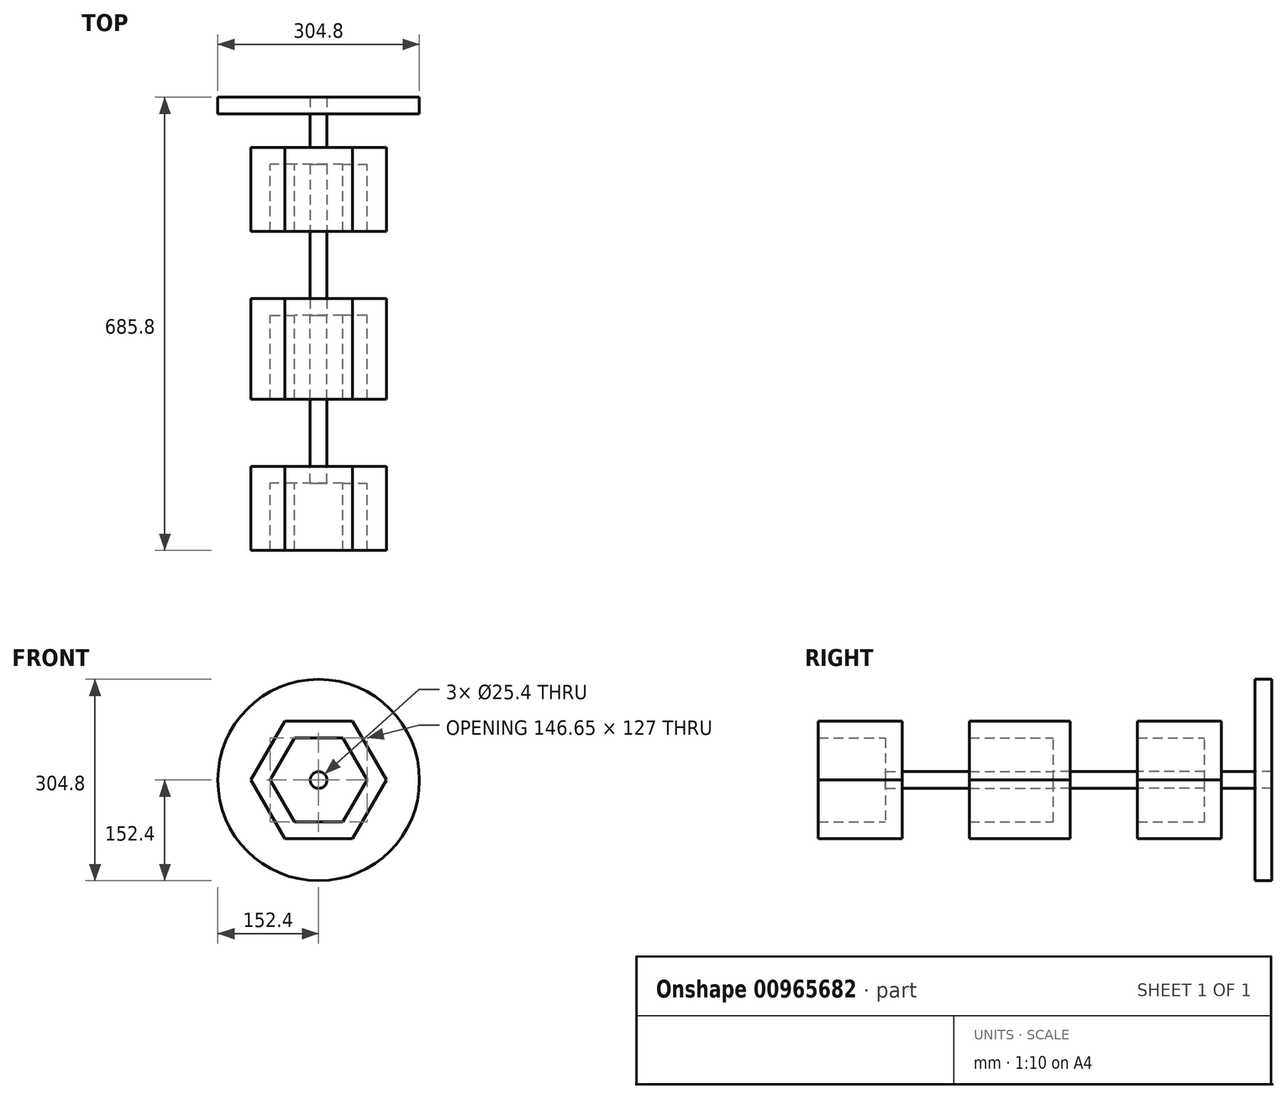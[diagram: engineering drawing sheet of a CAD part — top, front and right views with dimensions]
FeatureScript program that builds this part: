
annotation { "Feature Type Name" : "Feature", "Feature Type Description" : "" }
export const myFeature = defineFeature(function(context is Context, id is Id, definition is map)
    precondition{}
    {
        {
            var Q0;
            Q0=qCreatedBy(makeId("Front.planeOp"),FACE);
            var sketch = newSketch(context, id + "F0", { "sketchPlane" : qUnion([Q0])});
            skCircle(sketch, "E0", {"center": v(0, 0) * mm, "radius": 88.9 * mm});
            skCircle(sketch, "E1.cCircle", {"center": v(0, 0) * mm, "radius": 88.9 * mm, "construction": true});
            skLineSegment(sketch, "E1.0", {"start": v(51.33, -88.9) * mm, "end": v(-51.33, -88.9) * mm});
            skLineSegment(sketch, "E1.1", {"start": v(-51.33, -88.9) * mm, "end": v(-102.65, 0) * mm});
            skLineSegment(sketch, "E1.2", {"start": v(-102.65, 0) * mm, "end": v(-51.33, 88.9) * mm});
            skLineSegment(sketch, "E1.3", {"start": v(-51.33, 88.9) * mm, "end": v(51.33, 88.9) * mm});
            skLineSegment(sketch, "E1.4", {"start": v(51.33, 88.9) * mm, "end": v(102.65, 0) * mm});
            skLineSegment(sketch, "E1.5", {"start": v(102.65, 0) * mm, "end": v(51.33, -88.9) * mm});
            skPoint(sketch, "E1.0.midPoint", {"position": v(0, -88.9) * mm});
            skLineSegment(sketch, "E2.0", {"start": v(-36.66, 63.5) * mm, "end": v(36.66, 63.5) * mm});
            skLineSegment(sketch, "E3.0", {"start": v(36.66, 63.5) * mm, "end": v(73.32, 0) * mm});
            skLineSegment(sketch, "E4.0", {"start": v(73.32, 0) * mm, "end": v(36.66, -63.5) * mm});
            skLineSegment(sketch, "E5.0", {"start": v(36.66, -63.5) * mm, "end": v(-36.66, -63.5) * mm});
            skLineSegment(sketch, "E6.0", {"start": v(-36.66, -63.5) * mm, "end": v(-73.32, 0) * mm});
            skLineSegment(sketch, "E7.0", {"start": v(-73.32, 0) * mm, "end": v(-36.66, 63.5) * mm});
            skCircle(sketch, "E8", {"center": v(0, 0) * mm, "radius": 12.7 * mm});
            skSolve(sketch);
        }
        {
            var Q0;
            Q0 = qSketchRegion(id + "F0", true);
            var Q1;
            Q1=makeQuery(id+"F0.imprint","IMPRINT",FACE,{"disambiguationData":[TD([[makeQuery(id+"F0.imprint","IMPRINT",EDGE,{"derivedFrom":sQuery(id+"F0.wireOp",EDGE,"E2.0")}),-1.0]])]});
            extrude(context, id + "F1", {"entities" : qUnion([Q0, Q1]), "oppositeDirection" : true, "depth" : 25.4 * mm, "offsetDistance" : 25.4 * mm});
        }
        {
            var Q0;
            {var subQ0=sQuery(id+"F0.wireOp",EDGE,"E1.3");var subQ1=sQuery(id+"F0.wireOp",EDGE,"E0");var subQ2=makeQuery(id+"F0.imprint","INTERSECT",VERTEX,{"derivedFrom":[subQ1,subQ0]});Q0=makeQuery(id+"F0.imprint","IMPRINT",FACE,{"disambiguationData":[TD([[makeQuery(id+"F0.imprint","IMPRINT",EDGE,{"disambiguationData":[TD([[subQ2,-1.0]])],"derivedFrom":subQ1}),-1.0]])]});}
            var Q1;
            {var subQ0=sQuery(id+"F0.wireOp",EDGE,"E1.3");var subQ1=sQuery(id+"F0.wireOp",EDGE,"E0");var subQ2=makeQuery(id+"F0.imprint","INTERSECT",VERTEX,{"derivedFrom":[subQ1,subQ0]});Q1=makeQuery(id+"F0.imprint","IMPRINT",FACE,{"disambiguationData":[TD([[makeQuery(id+"F0.imprint","IMPRINT",EDGE,{"disambiguationData":[TD([[subQ2,1.0]])],"derivedFrom":subQ1}),-1.0]])]});}
            var Q2;
            {var subQ0=sQuery(id+"F0.wireOp",EDGE,"E1.4");var subQ1=sQuery(id+"F0.wireOp",EDGE,"E0");var subQ2=makeQuery(id+"F0.imprint","INTERSECT",VERTEX,{"derivedFrom":[subQ1,subQ0]});Q2=makeQuery(id+"F0.imprint","IMPRINT",FACE,{"disambiguationData":[TD([[makeQuery(id+"F0.imprint","IMPRINT",EDGE,{"disambiguationData":[TD([[subQ2,1.0]])],"derivedFrom":subQ1}),-1.0]])]});}
            var Q3;
            {var subQ0=sQuery(id+"F0.wireOp",EDGE,"E1.0");var subQ1=sQuery(id+"F0.wireOp",EDGE,"E0");var subQ2=makeQuery(id+"F0.imprint","INTERSECT",VERTEX,{"derivedFrom":[subQ1,subQ0]});Q3=makeQuery(id+"F0.imprint","IMPRINT",FACE,{"disambiguationData":[TD([[makeQuery(id+"F0.imprint","IMPRINT",EDGE,{"disambiguationData":[TD([[subQ2,-1.0]])],"derivedFrom":subQ1}),-1.0]])]});}
            var Q4;
            {var subQ0=sQuery(id+"F0.wireOp",EDGE,"E1.1");var subQ1=sQuery(id+"F0.wireOp",EDGE,"E0");var subQ2=makeQuery(id+"F0.imprint","INTERSECT",VERTEX,{"derivedFrom":[subQ1,subQ0]});Q4=makeQuery(id+"F0.imprint","IMPRINT",FACE,{"disambiguationData":[TD([[makeQuery(id+"F0.imprint","IMPRINT",EDGE,{"disambiguationData":[TD([[subQ2,-1.0]])],"derivedFrom":subQ1}),-1.0]])]});}
            var Q5;
            {var subQ0=sQuery(id+"F0.wireOp",EDGE,"E1.2");var subQ1=sQuery(id+"F0.wireOp",EDGE,"E0");var subQ2=makeQuery(id+"F0.imprint","INTERSECT",VERTEX,{"derivedFrom":[subQ1,subQ0]});Q5=makeQuery(id+"F0.imprint","IMPRINT",FACE,{"disambiguationData":[TD([[makeQuery(id+"F0.imprint","IMPRINT",EDGE,{"disambiguationData":[TD([[subQ2,-1.0]])],"derivedFrom":subQ1}),-1.0]])]});}
            var Q6;
            Q6=makeQuery(id+"F0.imprint","IMPRINT",FACE,{"disambiguationData":[TD([[makeQuery(id+"F0.imprint","IMPRINT",EDGE,{"derivedFrom":sQuery(id+"F0.wireOp",EDGE,"E2.0")}),1.0]])]});
            extrude(context, id + "F2", {"entities" : qUnion([Q0, Q1, Q2, Q3, Q4, Q5, Q6]), "operationType" : NewBodyOperationType.ADD, "depth" : 127 * mm, "offsetDistance" : 25.4 * mm});
        }
        {
            var Q0;
            Q0=makeQuery(id+"F0.imprint","IMPRINT",FACE,{"disambiguationData":[TD([[makeQuery(id+"F0.imprint","IMPRINT",EDGE,{"derivedFrom":sQuery(id+"F0.wireOp",EDGE,"E8")}),1.0]])]});
            extrude(context, id + "F3", {"entities" : qUnion([Q0]), "depth" : 228.6 * mm, "offsetDistance" : 25.4 * mm});
        }
        {
            var Q0;
            Q0=makeQuery(id+"F3.opExtrude","CAP_FACE",FACE,{"disambiguationData":[OSD([sQuery(id+"F0.wireOp",EDGE,"E8")])],"isStart":false});
            var sketch = newSketch(context, id + "F4", { "sketchPlane" : qUnion([Q0])});
            skCircle(sketch, "E9", {"center": v(0, 0) * mm, "radius": 88.9 * mm});
            skCircle(sketch, "E10.cCircle", {"center": v(0, 0) * mm, "radius": 88.9 * mm, "construction": true});
            skLineSegment(sketch, "E10.0", {"start": v(51.33, -88.9) * mm, "end": v(-51.33, -88.9) * mm});
            skLineSegment(sketch, "E10.1", {"start": v(-51.33, -88.9) * mm, "end": v(-102.65, 0) * mm});
            skLineSegment(sketch, "E10.2", {"start": v(-102.65, 0) * mm, "end": v(-51.33, 88.9) * mm});
            skLineSegment(sketch, "E10.3", {"start": v(-51.33, 88.9) * mm, "end": v(51.33, 88.9) * mm});
            skLineSegment(sketch, "E10.4", {"start": v(51.33, 88.9) * mm, "end": v(102.65, 0) * mm});
            skLineSegment(sketch, "E10.5", {"start": v(102.65, 0) * mm, "end": v(51.33, -88.9) * mm});
            skPoint(sketch, "E10.0.midPoint", {"position": v(0, -88.9) * mm});
            skLineSegment(sketch, "E11.0", {"start": v(-36.66, 63.5) * mm, "end": v(36.66, 63.5) * mm});
            skLineSegment(sketch, "E12.0", {"start": v(36.66, 63.5) * mm, "end": v(73.32, 0) * mm});
            skLineSegment(sketch, "E13.0", {"start": v(73.32, 0) * mm, "end": v(36.66, -63.5) * mm});
            skLineSegment(sketch, "E14.0", {"start": v(36.66, -63.5) * mm, "end": v(-36.66, -63.5) * mm});
            skLineSegment(sketch, "E15.0", {"start": v(-36.66, -63.5) * mm, "end": v(-73.32, 0) * mm});
            skLineSegment(sketch, "E16.0", {"start": v(-73.32, 0) * mm, "end": v(-36.66, 63.5) * mm});
            skSolve(sketch);
        }
        {
            var Q0;
            Q0=makeQuery(id+"F4.imprint","IMPRINT",FACE,{"disambiguationData":[TD([[makeQuery(id+"F4.imprint","IMPRINT",EDGE,{"derivedFrom":sQuery(id+"F4.wireOp",EDGE,"E11.0")}),1.0]])]});
            var Q1;
            Q1=makeQuery(id+"F4.imprint","IMPRINT",FACE,{"disambiguationData":[TD([[makeQuery(id+"F4.imprint","IMPRINT",EDGE,{"derivedFrom":sQuery(id+"F4.wireOp",EDGE,"E11.0")}),-1.0]])]});
            extrude(context, id + "F5", {"entities" : qUnion([Q0, Q1]), "depth" : 25.4 * mm, "offsetDistance" : 25.4 * mm});
        }
        {
            var Q0;
            {var subQ0=sQuery(id+"F4.wireOp",EDGE,"E10.3");var subQ1=sQuery(id+"F4.wireOp",EDGE,"E9");var subQ2=makeQuery(id+"F4.imprint","INTERSECT",VERTEX,{"derivedFrom":[subQ1,subQ0]});Q0=makeQuery(id+"F4.imprint","IMPRINT",FACE,{"disambiguationData":[TD([[makeQuery(id+"F4.imprint","IMPRINT",EDGE,{"disambiguationData":[TD([[subQ2,-1.0]])],"derivedFrom":subQ1}),-1.0]])]});}
            var Q1;
            {var subQ0=sQuery(id+"F4.wireOp",EDGE,"E10.3");var subQ1=sQuery(id+"F4.wireOp",EDGE,"E9");var subQ2=makeQuery(id+"F4.imprint","INTERSECT",VERTEX,{"derivedFrom":[subQ1,subQ0]});Q1=makeQuery(id+"F4.imprint","IMPRINT",FACE,{"disambiguationData":[TD([[makeQuery(id+"F4.imprint","IMPRINT",EDGE,{"disambiguationData":[TD([[subQ2,1.0]])],"derivedFrom":subQ1}),-1.0]])]});}
            var Q2;
            {var subQ0=sQuery(id+"F4.wireOp",EDGE,"E10.4");var subQ1=sQuery(id+"F4.wireOp",EDGE,"E9");var subQ2=makeQuery(id+"F4.imprint","INTERSECT",VERTEX,{"derivedFrom":[subQ1,subQ0]});Q2=makeQuery(id+"F4.imprint","IMPRINT",FACE,{"disambiguationData":[TD([[makeQuery(id+"F4.imprint","IMPRINT",EDGE,{"disambiguationData":[TD([[subQ2,1.0]])],"derivedFrom":subQ1}),-1.0]])]});}
            var Q3;
            {var subQ0=sQuery(id+"F4.wireOp",EDGE,"E10.0");var subQ1=sQuery(id+"F4.wireOp",EDGE,"E9");var subQ2=makeQuery(id+"F4.imprint","INTERSECT",VERTEX,{"derivedFrom":[subQ1,subQ0]});Q3=makeQuery(id+"F4.imprint","IMPRINT",FACE,{"disambiguationData":[TD([[makeQuery(id+"F4.imprint","IMPRINT",EDGE,{"disambiguationData":[TD([[subQ2,-1.0]])],"derivedFrom":subQ1}),-1.0]])]});}
            var Q4;
            {var subQ0=sQuery(id+"F4.wireOp",EDGE,"E10.1");var subQ1=sQuery(id+"F4.wireOp",EDGE,"E9");var subQ2=makeQuery(id+"F4.imprint","INTERSECT",VERTEX,{"derivedFrom":[subQ1,subQ0]});Q4=makeQuery(id+"F4.imprint","IMPRINT",FACE,{"disambiguationData":[TD([[makeQuery(id+"F4.imprint","IMPRINT",EDGE,{"disambiguationData":[TD([[subQ2,-1.0]])],"derivedFrom":subQ1}),-1.0]])]});}
            var Q5;
            {var subQ0=sQuery(id+"F4.wireOp",EDGE,"E10.2");var subQ1=sQuery(id+"F4.wireOp",EDGE,"E9");var subQ2=makeQuery(id+"F4.imprint","INTERSECT",VERTEX,{"derivedFrom":[subQ1,subQ0]});Q5=makeQuery(id+"F4.imprint","IMPRINT",FACE,{"disambiguationData":[TD([[makeQuery(id+"F4.imprint","IMPRINT",EDGE,{"disambiguationData":[TD([[subQ2,-1.0]])],"derivedFrom":subQ1}),-1.0]])]});}
            var Q6;
            Q6=makeQuery(id+"F4.imprint","IMPRINT",FACE,{"disambiguationData":[TD([[makeQuery(id+"F4.imprint","IMPRINT",EDGE,{"derivedFrom":sQuery(id+"F4.wireOp",EDGE,"E11.0")}),1.0]])]});
            extrude(context, id + "F6", {"entities" : qUnion([Q0, Q1, Q2, Q3, Q4, Q5, Q6]), "operationType" : NewBodyOperationType.ADD, "depth" : 127 * mm, "offsetDistance" : 25.4 * mm});
        }
        {
            var Q0;
            Q0=makeQuery(id+"F1.opExtrude","CAP_FACE",FACE,{"disambiguationData":[OSD([sQuery(id+"F0.wireOp",EDGE,"E1.0"),sQuery(id+"F0.wireOp",EDGE,"E1.1"),sQuery(id+"F0.wireOp",EDGE,"E1.2"),sQuery(id+"F0.wireOp",EDGE,"E1.3"),sQuery(id+"F0.wireOp",EDGE,"E1.4"),sQuery(id+"F0.wireOp",EDGE,"E1.5"),sQuery(id+"F0.wireOp",EDGE,"E8")])],"isStart":false});
            var sketch = newSketch(context, id + "F7", { "sketchPlane" : qUnion([Q0])});
            skCircle(sketch, "E17", {"center": v(0, 0) * mm, "radius": 12.7 * mm});
            skSolve(sketch);
        }
        {
            var Q0;
            Q0=makeQuery(id+"F7.imprint","IMPRINT",FACE,{"disambiguationData":[TD([[makeQuery(id+"F7.imprint","IMPRINT",EDGE,{"derivedFrom":sQuery(id+"F7.wireOp",EDGE,"E17")}),-1.0]])]});
            extrude(context, id + "F8", {"entities" : qUnion([Q0]), "depth" : 228.6 * mm, "offsetDistance" : 25.4 * mm});
        }
        {
            var Q0;
            Q0=makeQuery(id+"F8.opExtrude","CAP_FACE",FACE,{"disambiguationData":[OSD([sQuery(id+"F7.wireOp",EDGE,"E17")])],"isStart":false});
            var sketch = newSketch(context, id + "F9", { "sketchPlane" : qUnion([Q0])});
            skCircle(sketch, "E18", {"center": v(0, 0) * mm, "radius": 88.9 * mm});
            skCircle(sketch, "E19.cCircle", {"center": v(0, 0) * mm, "radius": 88.9 * mm, "construction": true});
            skLineSegment(sketch, "E19.0", {"start": v(-51.33, 88.9) * mm, "end": v(51.33, 88.9) * mm});
            skLineSegment(sketch, "E19.1", {"start": v(51.33, 88.9) * mm, "end": v(102.65, 0) * mm});
            skLineSegment(sketch, "E19.2", {"start": v(102.65, 0) * mm, "end": v(51.33, -88.9) * mm});
            skLineSegment(sketch, "E19.3", {"start": v(51.33, -88.9) * mm, "end": v(-51.33, -88.9) * mm});
            skLineSegment(sketch, "E19.4", {"start": v(-51.33, -88.9) * mm, "end": v(-102.65, 0) * mm});
            skLineSegment(sketch, "E19.5", {"start": v(-102.65, 0) * mm, "end": v(-51.33, 88.9) * mm});
            skPoint(sketch, "E19.0.midPoint", {"position": v(0, 88.9) * mm});
            skLineSegment(sketch, "E20.0", {"start": v(-36.66, 63.5) * mm, "end": v(36.66, 63.5) * mm});
            skLineSegment(sketch, "E21.0", {"start": v(36.66, 63.5) * mm, "end": v(73.32, 0) * mm});
            skLineSegment(sketch, "E22.0", {"start": v(73.32, 0) * mm, "end": v(36.66, -63.5) * mm});
            skLineSegment(sketch, "E23.0", {"start": v(36.66, -63.5) * mm, "end": v(-36.66, -63.5) * mm});
            skLineSegment(sketch, "E24.0", {"start": v(-36.66, -63.5) * mm, "end": v(-73.32, 0) * mm});
            skLineSegment(sketch, "E25.0", {"start": v(-73.32, 0) * mm, "end": v(-36.66, 63.5) * mm});
            skSolve(sketch);
        }
        {
            var Q0;
            Q0=makeQuery(id+"F9.imprint","IMPRINT",FACE,{"disambiguationData":[TD([[makeQuery(id+"F9.imprint","IMPRINT",EDGE,{"derivedFrom":sQuery(id+"F9.wireOp",EDGE,"E18")}),1.0]])]});
            var Q1;
            Q1=makeQuery(id+"F9.imprint","IMPRINT",FACE,{"disambiguationData":[TD([[makeQuery(id+"F9.imprint","IMPRINT",EDGE,{"derivedFrom":sQuery(id+"F9.wireOp",EDGE,"E20.0")}),-1.0]])]});
            extrude(context, id + "F10", {"entities" : qUnion([Q0, Q1]), "oppositeDirection" : true, "depth" : 25.4 * mm, "offsetDistance" : 25.4 * mm});
        }
        {
            var Q0;
            {var subQ0=sQuery(id+"F9.wireOp",EDGE,"E19.0");var subQ1=sQuery(id+"F9.wireOp",EDGE,"E18");var subQ2=makeQuery(id+"F9.imprint","INTERSECT",VERTEX,{"derivedFrom":[subQ1,subQ0]});Q0=makeQuery(id+"F9.imprint","IMPRINT",FACE,{"disambiguationData":[TD([[makeQuery(id+"F9.imprint","IMPRINT",EDGE,{"disambiguationData":[TD([[subQ2,1.0]])],"derivedFrom":subQ1}),-1.0]])]});}
            var Q1;
            {var subQ0=sQuery(id+"F9.wireOp",EDGE,"E19.0");var subQ1=sQuery(id+"F9.wireOp",EDGE,"E18");var subQ2=makeQuery(id+"F9.imprint","INTERSECT",VERTEX,{"derivedFrom":[subQ1,subQ0]});Q1=makeQuery(id+"F9.imprint","IMPRINT",FACE,{"disambiguationData":[TD([[makeQuery(id+"F9.imprint","IMPRINT",EDGE,{"disambiguationData":[TD([[subQ2,-1.0]])],"derivedFrom":subQ1}),-1.0]])]});}
            var Q2;
            {var subQ0=sQuery(id+"F9.wireOp",EDGE,"E19.5");var subQ1=sQuery(id+"F9.wireOp",EDGE,"E18");var subQ2=makeQuery(id+"F9.imprint","INTERSECT",VERTEX,{"derivedFrom":[subQ1,subQ0]});Q2=makeQuery(id+"F9.imprint","IMPRINT",FACE,{"disambiguationData":[TD([[makeQuery(id+"F9.imprint","IMPRINT",EDGE,{"disambiguationData":[TD([[subQ2,-1.0]])],"derivedFrom":subQ1}),-1.0]])]});}
            var Q3;
            {var subQ0=sQuery(id+"F9.wireOp",EDGE,"E19.3");var subQ1=sQuery(id+"F9.wireOp",EDGE,"E18");var subQ2=makeQuery(id+"F9.imprint","INTERSECT",VERTEX,{"derivedFrom":[subQ1,subQ0]});Q3=makeQuery(id+"F9.imprint","IMPRINT",FACE,{"disambiguationData":[TD([[makeQuery(id+"F9.imprint","IMPRINT",EDGE,{"disambiguationData":[TD([[subQ2,-1.0]])],"derivedFrom":subQ1}),-1.0]])]});}
            var Q4;
            {var subQ0=sQuery(id+"F9.wireOp",EDGE,"E19.4");var subQ1=sQuery(id+"F9.wireOp",EDGE,"E18");var subQ2=makeQuery(id+"F9.imprint","INTERSECT",VERTEX,{"derivedFrom":[subQ1,subQ0]});Q4=makeQuery(id+"F9.imprint","IMPRINT",FACE,{"disambiguationData":[TD([[makeQuery(id+"F9.imprint","IMPRINT",EDGE,{"disambiguationData":[TD([[subQ2,-1.0]])],"derivedFrom":subQ1}),-1.0]])]});}
            var Q5;
            {var subQ0=sQuery(id+"F9.wireOp",EDGE,"E19.1");var subQ1=sQuery(id+"F9.wireOp",EDGE,"E18");var subQ2=makeQuery(id+"F9.imprint","INTERSECT",VERTEX,{"derivedFrom":[subQ1,subQ0]});Q5=makeQuery(id+"F9.imprint","IMPRINT",FACE,{"disambiguationData":[TD([[makeQuery(id+"F9.imprint","IMPRINT",EDGE,{"disambiguationData":[TD([[subQ2,1.0]])],"derivedFrom":subQ1}),-1.0]])]});}
            var Q6;
            Q6=makeQuery(id+"F9.imprint","IMPRINT",FACE,{"disambiguationData":[TD([[makeQuery(id+"F9.imprint","IMPRINT",EDGE,{"derivedFrom":sQuery(id+"F9.wireOp",EDGE,"E20.0")}),1.0]])]});
            extrude(context, id + "F11", {"entities" : qUnion([Q0, Q1, Q2, Q3, Q4, Q5, Q6]), "operationType" : NewBodyOperationType.ADD, "oppositeDirection" : true, "depth" : 127 * mm, "offsetDistance" : 25.4 * mm});
        }
        {
            var Q0;
            Q0=makeQuery(id+"F8.opExtrude","CAP_FACE",FACE,{"disambiguationData":[OSD([sQuery(id+"F7.wireOp",EDGE,"E17")])],"isStart":false});
            var sketch = newSketch(context, id + "F12", { "sketchPlane" : qUnion([Q0])});
            skCircle(sketch, "E26", {"center": v(0, 0) * mm, "radius": 12.7 * mm});
            skSolve(sketch);
        }
        {
            var Q0;
            Q0=makeQuery(id+"F12.imprint","IMPRINT",FACE,{"disambiguationData":[TD([[makeQuery(id+"F12.imprint","IMPRINT",EDGE,{"derivedFrom":sQuery(id+"F12.wireOp",EDGE,"E26")}),-1.0]])]});
            extrude(context, id + "F13", {"entities" : qUnion([Q0]), "operationType" : NewBodyOperationType.ADD, "depth" : 50.8 * mm, "offsetDistance" : 25.4 * mm});
        }
        {
            var Q0;
            Q0=makeQuery(id+"F13.opExtrude","CAP_FACE",FACE,{"disambiguationData":[OSD([sQuery(id+"F12.wireOp",EDGE,"E26")])],"isStart":false});
            var sketch = newSketch(context, id + "F14", { "sketchPlane" : qUnion([Q0])});
            skCircle(sketch, "E27", {"center": v(0, 0) * mm, "radius": 152.4 * mm});
            skSolve(sketch);
        }
        {
            var Q0;
            Q0=makeQuery(id+"F14.imprint","IMPRINT",FACE,{"disambiguationData":[TD([[makeQuery(id+"F14.imprint","IMPRINT",EDGE,{"derivedFrom":sQuery(id+"F14.wireOp",EDGE,"E27")}),1.0]])]});
            extrude(context, id + "F15", {"entities" : qUnion([Q0]), "depth" : 25.4 * mm, "offsetDistance" : 25.4 * mm});
        }
        {
            var Q0;
            Q0=makeQuery(id+"F14.imprint","IMPRINT",FACE,{"disambiguationData":[TD([[makeQuery(id+"F14.imprint","IMPRINT",EDGE,{"derivedFrom":sQuery(id+"F14.wireOp",EDGE,"E27")}),1.0]])]});
            var Q1;
            Q1=makeQuery(id+"F14.imprint","IMPRINT",FACE,{"disambiguationData":[TD([[makeQuery(id+"F14.imprint","IMPRINT",EDGE,{"derivedFrom":makeQuery(id+"F13.opExtrude","CAP_EDGE",EDGE,{"disambiguationData":[OSD([sQuery(id+"F12.wireOp",EDGE,"E26")])],"isStart":false})}),-1.0]])]});
            extrude(context, id + "F16", {"entities" : qUnion([Q0, Q1]), "depth" : 25.4 * mm, "offsetDistance" : 25.4 * mm});
        }
    });
